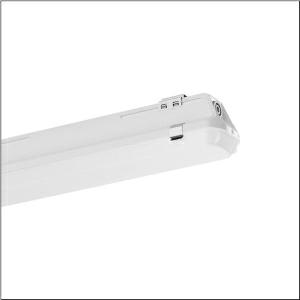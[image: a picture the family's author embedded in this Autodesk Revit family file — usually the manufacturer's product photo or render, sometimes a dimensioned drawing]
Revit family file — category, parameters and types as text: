
# Revit family: monsun_r__21_parking_51fg207l430j_46f3
name_source: partatom
category: Lighting Fixtures
units: mm (PartAtom-declared; Revit-internal decimal feet)

## family parameters
Cut with Voids When Loaded = No
Host = Face
Light Source = No
Part Type = Normal
Room Calculation Point = No
Round Connector Dimension = Use Diameter
Shared = No

## types (1)
- Monsun® 21 parking (1 x LED, 4030 lm, 27.2 W, 4000K)
    Apparent Load = 27 VA
    CIE Flux Codes = 45 75 93 94 100
    Color Rendering = 80
    Color Temperature = 4000K
    Default Elevation = 1800 mm
    Description = Monsun® 21 parking, damp-proof luminaire, chain hanger, primary optical cover: enclosure, of PC, light emission: direct distribution, primary light characteristic: symmetric, installation type: suspended mounting, surface-mounted, horizontal mounting, vertical mounting, LED, rated luminous flux: 4.030lm, luminous efficacy: 149lm/W, light colour: 840, colour temperature: 4000K, control gear: ECG, with terminal, 3-pole, max. 2.5mm², mains connection: 220..240V, AC, 50/60Hz, rated input power: 27W, housing, of glass-fibre reinforced plastic, uncoated, bright grey, incl. chain hanger, length: 1.299mm, width: 90mm, height: 88mm, clip for enclosure, of stainless steel (V2A), ceiling mounting element, of stainless steel (V2A), chain hanger, of stainless steel (V2A), protection rating (complete): IP66, insulation class (complete): insulation class I (protective earthing), certification: CE, ENEC, VDE, UKCA, protection symbol: D, impact resistance: IK08, permissible operating ambient temperature: -25..+35°C, standard: EN 50419, EN 60598-2-1, corresponds to IFS (International Featured Standards) requirements for safety and quality in the food industry, for indoor or canopied outdoor use, no direct snow, no direct sun, no direct rain, contact your sales advisor before using the luminaires in applications with unclear chemical exposure, large temperature fluctuations or condensation-forming humidity, LABS conformity tested according to VDMA 24364:2018-05, packaging unit: 1 piece
    Height = 88 mm
    Lamp = 1 x LED
    Lamp Light Flux = 4030 lm
    Lamp Power = 27.2 W
    Lamp count = 1
    Length = 1299 mm
    Luminous efficacy = 148 lm/W
    Manufacturer = Siteco
    ModVariant = No
    Model = 51FG207L430J
    Mounting Place = Ceiling
    Mounting Type = Surface mounted
    Number of Poles = 1
    OnlyDefault = Yes
    Power Factor = 1
    Product Name = Monsun® 21 parking
    Product group = damp-proof luminaire
    ProductGroupID = 300
    Protection Class = Protection class I
    Protection Degree = IP 66
    RLX_Detail_Level = 1
    RLX_Emergency_Light_Flux = 0 lm
    RLX_Emergency_Type = 0
    RLX_Emergency_Type_DB = No
    RlxData = <blob elided: 89829 chars, md5=4c0195d8>
    Socket = socket
    Standby Power = 0 W
    System Light Flux = 4030 lm
    System Power = 27 W
    Type Comments = Product without accessories
    Type Image = l_1006717.jpg
    URL = http://relux.com
    VarID = ---
    Voltage = 0 V
    Weight = 0.00 kg
    Width = 90 mm

## geometry (parser evidence)
native form markers: Blend x4, Sweep x12
no freeform markers — native parametric forms only
